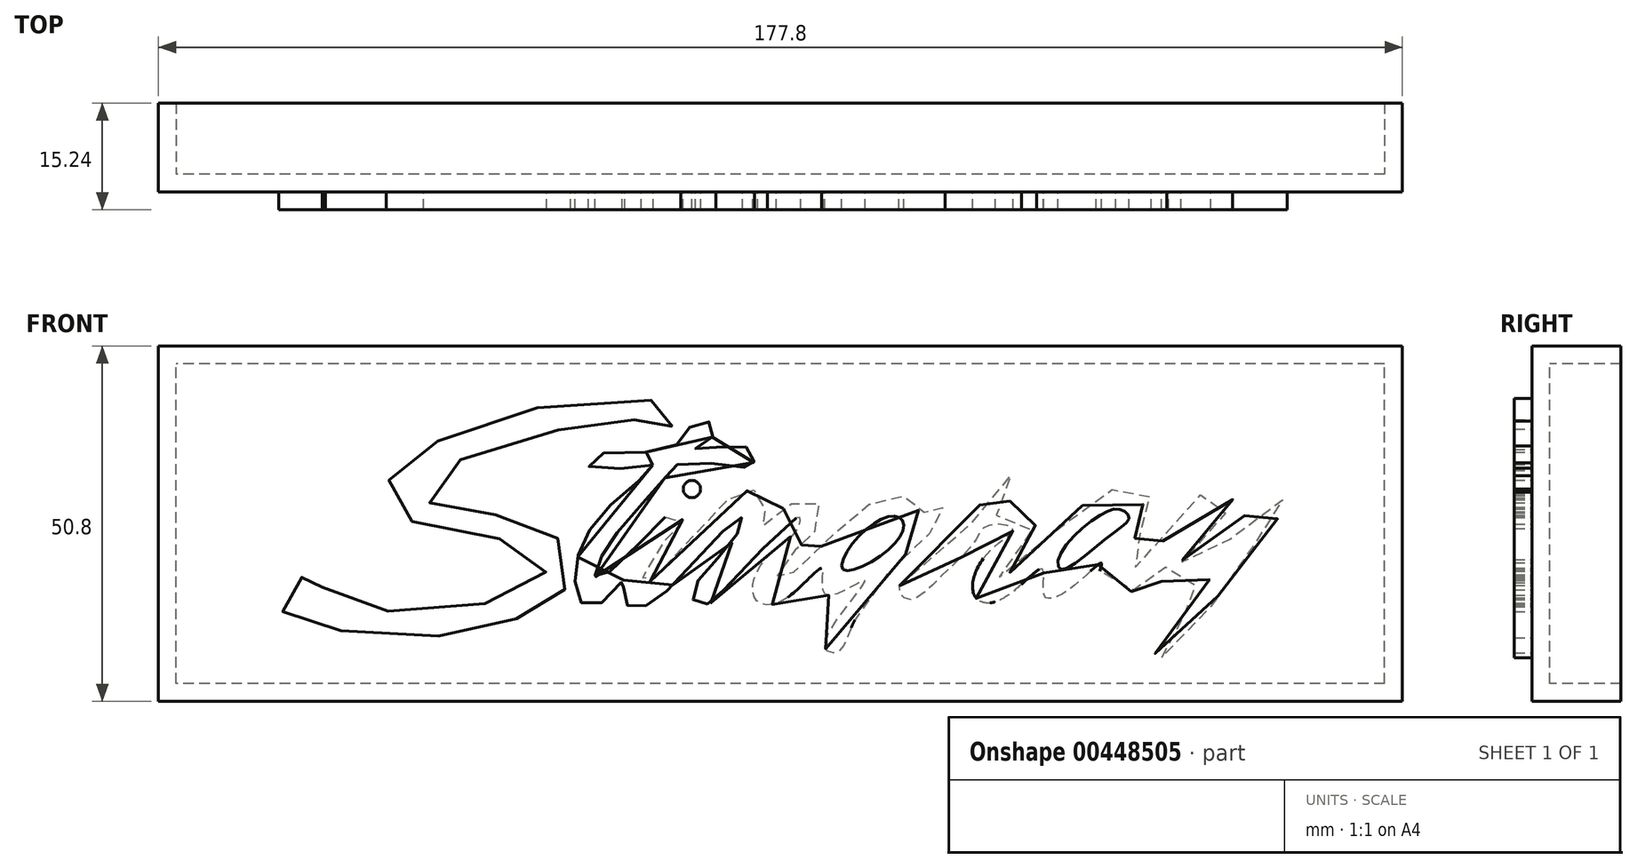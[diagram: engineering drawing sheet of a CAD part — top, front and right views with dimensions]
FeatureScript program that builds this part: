
annotation { "Feature Type Name" : "Feature", "Feature Type Description" : "" }
export const myFeature = defineFeature(function(context is Context, id is Id, definition is map)
    precondition{}
    {
        {
            var Q0;
            Q0=qCreatedBy(makeId("Front.planeOp"),FACE);
            var sketch = newSketch(context, id + "F0", { "sketchPlane" : qUnion([Q0])});
            skFitSpline(sketch, "E0", {"points": [v(-104.36, 39.31) * mm, v(-103.13, 40.98) * mm, v(-107, 43) * mm, v(-126.92, 41.24) * mm, v(-140.09, 36.06) * mm, v(-144.39, 32.55) * mm, v(-145, 28.25) * mm, v(-141.23, 25.62) * mm, v(-129.12, 23.25) * mm, v(-122.53, 20.09) * mm, v(-123.15, 17.37) * mm, v(-131.22, 13.94) * mm, v(-145.8, 12.98) * mm, v(-154.3, 15.61) * mm, v(-153.96, 17.9) * mm, v(-154.48, 18.68) * mm, v(-157.9, 17.46) * mm, v(-160.45, 15.61) * mm, v(-159.84, 12.54) * mm, v(-156.59, 11.14) * mm, v(-144.12, 9.12) * mm, v(-131.3, 10.43) * mm, v(-124.46, 12.63) * mm, v(-120.34, 15.09) * mm, v(-118.93, 19.56) * mm, v(-120.95, 23.51) * mm, v(-126.83, 26.06) * mm, v(-135, 27.46) * mm, v(-139.56, 28.87) * mm, v(-138.95, 31.85) * mm, v(-124.55, 37.9) * mm, v(-115.07, 39.66) * mm, v(-107.35, 40.01) * mm, v(-105.77, 38.96) * mm, v(-104.36, 39.31) * mm]});
            skFitSpline(sketch, "E1", {"points": [v(-107.17, 33.78) * mm, v(-115.86, 33.25) * mm, v(-115.69, 35.01) * mm, v(-104.71, 36.06) * mm, v(-102.17, 38.87) * mm, v(-99.27, 40.01) * mm, v(-98.22, 38.35) * mm, v(-101.03, 36.15) * mm, v(-97.25, 36.41) * mm, v(-92.78, 35.71) * mm, v(-93.04, 33.52) * mm, v(-94.62, 33.6) * mm, v(-103.66, 33.87) * mm, v(-104.89, 32.64) * mm, v(-111.47, 25.1) * mm, v(-114.9, 19.83) * mm, v(-115.25, 17.72) * mm, v(-110.95, 20.62) * mm, v(-103.92, 26.93) * mm, v(-102.87, 25.7) * mm, v(-103.48, 25) * mm, v(-107.35, 20.35) * mm, v(-108.66, 16.58) * mm, v(-102.52, 22.28) * mm, v(-95.94, 29.22) * mm, v(-93.13, 30.18) * mm, v(-90.76, 29.4) * mm, v(-92.16, 24.74) * mm, v(-90.06, 26.32) * mm, v(-85.84, 28.78) * mm, v(-83.2, 27.99) * mm, v(-84, 24.3) * mm, v(-86.1, 22.2) * mm, v(-88.65, 19.47) * mm, v(-89.35, 17.02) * mm, v(-83.03, 22.2) * mm, v(-75.92, 28.34) * mm, v(-71, 29.22) * mm, v(-68.55, 26.93) * mm, v(-67.06, 28.34) * mm, v(-65.4, 26.93) * mm, v(-69.34, 22.55) * mm, v(-78.38, 11.4) * mm, v(-80.84, 7) * mm, v(-82.6, 8.06) * mm, v(-76.8, 17.2) * mm, v(-80.05, 15.7) * mm, v(-82.6, 15.44) * mm, v(-82.86, 17.8) * mm, v(-83.03, 19.04) * mm, v(-88.48, 14.47) * mm, v(-92.34, 14.47) * mm, v(-92.43, 18.16) * mm, v(-88.91, 22.46) * mm, v(-86.46, 24.65) * mm, v(-86.28, 26.32) * mm, v(-98.48, 14.38) * mm, v(-99.45, 13.94) * mm, v(-101.3, 14.38) * mm, v(-100.68, 17.28) * mm, v(-95.85, 22.72) * mm, v(-94.36, 26.23) * mm, v(-98.04, 23.42) * mm, v(-106.64, 14.47) * mm, v(-109.45, 13.5) * mm, v(-111.47, 14.47) * mm, v(-111.12, 17.54) * mm, v(-113.75, 14.56) * mm, v(-117.27, 14.03) * mm, v(-118.23, 18.07) * mm, v(-116.74, 23.51) * mm, v(-110.95, 30.1) * mm, v(-107.17, 33.78) * mm]});
            skCircle(sketch, "E2", {"center": v(-101.55, 30.36) * mm, "radius": 1.24 * mm});
            skFitSpline(sketch, "E3", {"points": [v(-71.89, 16.49) * mm, v(-62.5, 24.3) * mm, v(-59.86, 29.3) * mm, v(-56.09, 32.29) * mm, v(-54.5, 30.62) * mm, v(-58.2, 26.67) * mm, v(-53.98, 27.11) * mm, v(-52.31, 25.62) * mm, v(-55.2, 22.28) * mm, v(-58.1, 17.8) * mm, v(-53.37, 20.35) * mm, v(-48.63, 25.35) * mm, v(-43.8, 29.3) * mm, v(-40.02, 30) * mm, v(-37.57, 27.72) * mm, v(-36.07, 29.3) * mm, v(-33.7, 28.34) * mm, v(-36.95, 24.74) * mm, v(-40.9, 18.25) * mm, v(-35.81, 21.14) * mm, v(-28.35, 29.83) * mm, v(-24.49, 29.66) * mm, v(-24.84, 27.37) * mm, v(-27.82, 25.27) * mm, v(-31.5, 19.91) * mm, v(-31.33, 18.68) * mm, v(-25.36, 22.28) * mm, v(-19.48, 29.92) * mm, v(-16.5, 27.99) * mm, v(-16.94, 27.02) * mm, v(-21.77, 21.67) * mm, v(-25.01, 17.02) * mm, v(-30.37, 9.38) * mm, v(-33.97, 6.22) * mm, v(-35.9, 7.8) * mm, v(-32.21, 11.4) * mm, v(-27.38, 17.98) * mm, v(-29.23, 16.75) * mm, v(-33.35, 16.05) * mm, v(-34.4, 17.37) * mm, v(-33.44, 20.26) * mm, v(-36.16, 17.9) * mm, v(-40.11, 15.09) * mm, v(-43.7, 15.7) * mm, v(-43, 19.74) * mm, v(-46.96, 16.49) * mm, v(-51.17, 15.09) * mm, v(-51.43, 18.86) * mm, v(-56.61, 15) * mm, v(-60.47, 14.38) * mm, v(-61.44, 16.58) * mm, v(-58.72, 21.76) * mm, v(-55.65, 24.74) * mm, v(-59.33, 25.1) * mm, v(-61, 22.99) * mm, v(-66, 17.8) * mm, v(-70.57, 14.56) * mm, v(-71.89, 16.49) * mm]});
            skFitSpline(sketch, "E4", {"points": [v(-48.71, 18.86) * mm, v(-48.98, 20.88) * mm, v(-43, 26.76) * mm, v(-40.11, 27.37) * mm, v(-39.06, 26.23) * mm, v(-42.04, 23.51) * mm, v(-48.71, 18.86) * mm]});
            skFitSpline(sketch, "E5", {"points": [v(-79.96, 18.86) * mm, v(-77.94, 23.34) * mm, v(-72.59, 26.5) * mm, v(-71.27, 25.27) * mm, v(-74.34, 20.97) * mm, v(-79.96, 18.86) * mm]});
            skSolve(sketch);
        }
        {
            var Q0;
            Q0=qCreatedBy(makeId("Front.planeOp"),FACE);
            var sketch = newSketch(context, id + "F1", { "sketchPlane" : qUnion([Q0])});
            skLineSegment(sketch, "E6.bottom", {"start": v(0, 0) * mm, "end": v(-177.8, 0) * mm});
            skLineSegment(sketch, "E6.top", {"start": v(0, 50.8) * mm, "end": v(-177.8, 50.8) * mm});
            skLineSegment(sketch, "E6.left", {"start": v(0, 0) * mm, "end": v(0, 50.8) * mm});
            skLineSegment(sketch, "E6.right", {"start": v(-177.8, 0) * mm, "end": v(-177.8, 50.8) * mm});
            skSolve(sketch);
        }
        {
            var Q0;
            Q0=makeQuery(id+"F1.imprint","IMPRINT",FACE,{"disambiguationData":[TD([[makeQuery(id+"F1.imprint","IMPRINT",EDGE,{"derivedFrom":sQuery(id+"F1.wireOp",EDGE,"E6.bottom")}),-1.0]])]});
            extrude(context, id + "F2", {"entities" : qUnion([Q0]), "oppositeDirection" : true, "depth" : 12.7 * mm, "offsetDistance" : 25.4 * mm});
        }
        {
            var Q0;
            Q0=makeQuery(id+"F2.opExtrude","CAP_FACE",FACE,{"disambiguationData":[OSD([sQuery(id+"F1.wireOp",EDGE,"E6.bottom"),sQuery(id+"F1.wireOp",EDGE,"E6.top"),sQuery(id+"F1.wireOp",EDGE,"E6.left"),sQuery(id+"F1.wireOp",EDGE,"E6.right")])],"isStart":false});
            shell(context, id + "F3", {"entities" : qUnion([Q0]), "thickness" : 2.54 * mm});
        }
        {
            var Q0;
            Q0=makeQuery(id+"F0.imprint","IMPRINT",FACE,{"disambiguationData":[TD([[makeQuery(id+"F0.imprint","IMPRINT",EDGE,{"derivedFrom":sQuery(id+"F0.wireOp",EDGE,"E0")}),1.0]])]});
            var Q1;
            Q1=makeQuery(id+"F0.imprint","IMPRINT",FACE,{"disambiguationData":[TD([[makeQuery(id+"F0.imprint","IMPRINT",EDGE,{"derivedFrom":sQuery(id+"F0.wireOp",EDGE,"E1")}),-1.0]])]});
            var Q2;
            Q2=makeQuery(id+"F0.imprint","IMPRINT",FACE,{"disambiguationData":[TD([[makeQuery(id+"F0.imprint","IMPRINT",EDGE,{"derivedFrom":sQuery(id+"F0.wireOp",EDGE,"E2")}),1.0]])]});
            var Q3;
            Q3=makeQuery(id+"F0.imprint","IMPRINT",FACE,{"disambiguationData":[TD([[makeQuery(id+"F0.imprint","IMPRINT",EDGE,{"derivedFrom":sQuery(id+"F0.wireOp",EDGE,"E3")}),-1.0]])]});
            extrude(context, id + "F4", {"entities" : qUnion([Q0, Q1, Q2, Q3]), "operationType" : NewBodyOperationType.ADD, "depth" : 2.54 * mm});
        }
    });
